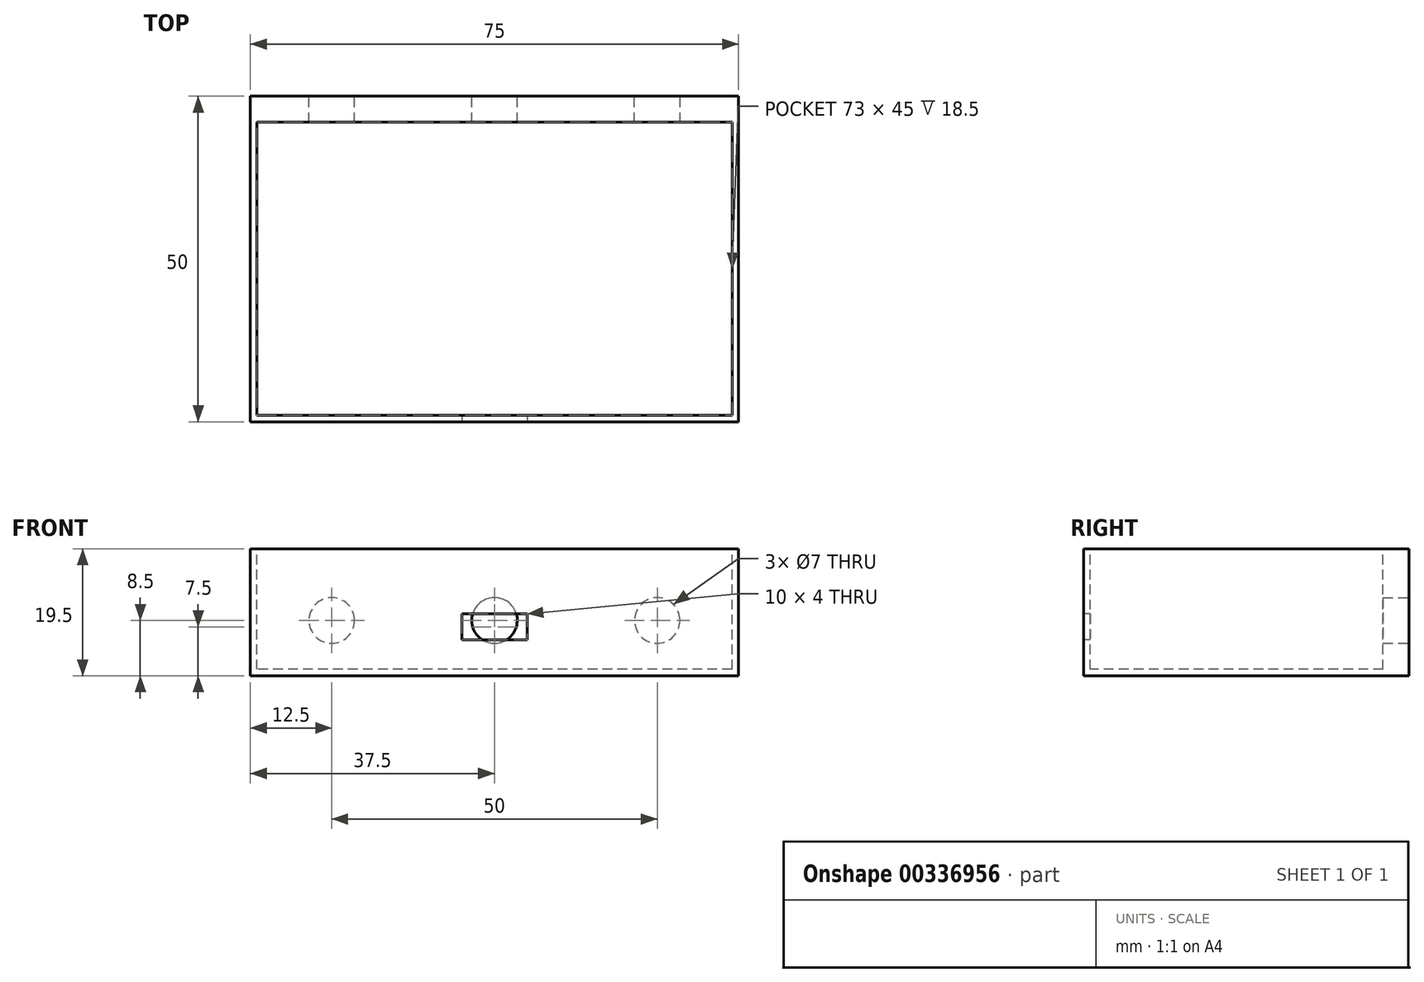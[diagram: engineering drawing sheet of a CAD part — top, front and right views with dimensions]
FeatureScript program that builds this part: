
annotation { "Feature Type Name" : "Feature", "Feature Type Description" : "" }
export const myFeature = defineFeature(function(context is Context, id is Id, definition is map)
    precondition{}
    {
        {
            assignVariable(context, id + "F0", {"name" : "floor_thickness", "anyValue" : 1});
        }
        {
            assignVariable(context, id + "F1", {"name" : "box_depth", "anyValue" : 17.5});
        }
        {
            var Q0;
            Q0=qCreatedBy(makeId("Top.planeOp"),FACE);
            var sketch = newSketch(context, id + "F2", { "sketchPlane" : qUnion([Q0])});
            skLineSegment(sketch, "E0.bottom", {"start": v(37.5, 25) * mm, "end": v(-37.5, 25) * mm});
            skLineSegment(sketch, "E0.top", {"start": v(37.5, -25) * mm, "end": v(-37.5, -25) * mm});
            skLineSegment(sketch, "E0.left", {"start": v(37.5, 25) * mm, "end": v(37.5, -25) * mm});
            skLineSegment(sketch, "E0.right", {"start": v(-37.5, 25) * mm, "end": v(-37.5, -25) * mm});
            skPoint(sketch, "E0.middle", {"position": v(0, 0) * mm});
            skSolve(sketch);
        }
        {
            var Q0;
            Q0 = qSketchRegion(id + "F2", true);
            extrude(context, id + "F3", {"entities" : qUnion([Q0]), "depth" : (getVariable(context, 'box_depth') + (getVariable(context, 'floor_thickness') * 2)) * mm});
        }
        {
            var Q0;
            Q0=makeQuery(id+"F3.opExtrude","CAP_FACE",FACE,{"disambiguationData":[OSD([sQuery(id+"F2.wireOp",EDGE,"E0.bottom"),sQuery(id+"F2.wireOp",EDGE,"E0.top"),sQuery(id+"F2.wireOp",EDGE,"E0.left"),sQuery(id+"F2.wireOp",EDGE,"E0.right")])],"isStart":false});
            var sketch = newSketch(context, id + "F4", { "sketchPlane" : qUnion([Q0])});
            skLineSegment(sketch, "E1.bottom", {"start": v(36.5, 21) * mm, "end": v(-36.5, 21) * mm});
            skLineSegment(sketch, "E1.top", {"start": v(36.5, -24) * mm, "end": v(-36.5, -24) * mm});
            skLineSegment(sketch, "E1.left", {"start": v(36.5, 21) * mm, "end": v(36.5, -24) * mm});
            skLineSegment(sketch, "E1.right", {"start": v(-36.5, 21) * mm, "end": v(-36.5, -24) * mm});
            skPoint(sketch, "E1.middle", {"position": v(0, 0) * mm});
            skSolve(sketch);
        }
        {
            var Q0;
            Q0=makeQuery(id+"F4.imprint","IMPRINT",FACE,{"disambiguationData":[TD([[makeQuery(id+"F4.imprint","IMPRINT",EDGE,{"derivedFrom":sQuery(id+"F4.wireOp",EDGE,"E1.bottom")}),1.0]])]});
            extrude(context, id + "F5", {"entities" : qUnion([Q0]), "operationType" : NewBodyOperationType.REMOVE, "oppositeDirection" : true, "depth" : (getVariable(context, 'box_depth') + getVariable(context, 'floor_thickness')) * mm});
        }
        {
            var Q0;
            Q0=makeQuery(id+"F3.opExtrude","SWEPT_FACE",FACE,{"disambiguationData":[OSD([sQuery(id+"F2.wireOp",EDGE,"E0.top")])]});
            var sketch = newSketch(context, id + "F6", { "sketchPlane" : qUnion([Q0])});
            skLineSegment(sketch, "E2", {"start": v(0, 0) * mm, "end": v(0, 7.5) * mm, "construction": true});
            skPoint(sketch, "E2.endSnap0", {"position": v(0, 0) * mm});
            skLineSegment(sketch, "E3.bottom", {"start": v(5, 9.5) * mm, "end": v(-5, 9.5) * mm});
            skLineSegment(sketch, "E3.top", {"start": v(5, 5.5) * mm, "end": v(-5, 5.5) * mm});
            skLineSegment(sketch, "E3.left", {"start": v(5, 9.5) * mm, "end": v(5, 5.5) * mm});
            skLineSegment(sketch, "E3.right", {"start": v(-5, 9.5) * mm, "end": v(-5, 5.5) * mm});
            skPoint(sketch, "E3.middle", {"position": v(0, 7.5) * mm});
            skSolve(sketch);
        }
        {
            var Q0;
            Q0=makeQuery(id+"F6.imprint","IMPRINT",FACE,{"disambiguationData":[TD([[makeQuery(id+"F6.imprint","IMPRINT",EDGE,{"derivedFrom":sQuery(id+"F6.wireOp",EDGE,"E3.bottom")}),1.0]])]});
            extrude(context, id + "F7", {"entities" : qUnion([Q0]), "operationType" : NewBodyOperationType.REMOVE, "endBound" : BoundingType.UP_TO_NEXT, "oppositeDirection" : true, "depth" : 25 * mm});
        }
        {
            var Q0;
            Q0=makeQuery(id+"F3.opExtrude","SWEPT_FACE",FACE,{"disambiguationData":[OSD([sQuery(id+"F2.wireOp",EDGE,"E0.bottom")])]});
            var sketch = newSketch(context, id + "F8", { "sketchPlane" : qUnion([Q0])});
            skLineSegment(sketch, "E4", {"start": v(0, 0) * mm, "end": v(0, 8.5) * mm, "construction": true});
            skLineSegment(sketch, "E5", {"start": v(0, 8.5) * mm, "end": v(25, 8.5) * mm, "construction": true});
            skLineSegment(sketch, "E6", {"start": v(0, 8.5) * mm, "end": v(-25, 8.5) * mm, "construction": true});
            skCircle(sketch, "E7", {"center": v(-25, 8.5) * mm, "radius": 3.5 * mm});
            skCircle(sketch, "E8", {"center": v(0, 8.5) * mm, "radius": 3.5 * mm});
            skCircle(sketch, "E9", {"center": v(25, 8.5) * mm, "radius": 3.5 * mm});
            skSolve(sketch);
        }
        {
            var Q0;
            Q0=makeQuery(id+"F8.imprint","IMPRINT",FACE,{"disambiguationData":[TD([[makeQuery(id+"F8.imprint","IMPRINT",EDGE,{"derivedFrom":sQuery(id+"F8.wireOp",EDGE,"E7")}),1.0]])]});
            var Q1;
            Q1=makeQuery(id+"F8.imprint","IMPRINT",FACE,{"disambiguationData":[TD([[makeQuery(id+"F8.imprint","IMPRINT",EDGE,{"derivedFrom":sQuery(id+"F8.wireOp",EDGE,"E8")}),1.0]])]});
            var Q2;
            Q2=makeQuery(id+"F8.imprint","IMPRINT",FACE,{"disambiguationData":[TD([[makeQuery(id+"F8.imprint","IMPRINT",EDGE,{"derivedFrom":sQuery(id+"F8.wireOp",EDGE,"E9")}),1.0]])]});
            extrude(context, id + "F9", {"entities" : qUnion([Q0, Q1, Q2]), "operationType" : NewBodyOperationType.REMOVE, "endBound" : BoundingType.UP_TO_NEXT, "oppositeDirection" : true, "depth" : 25 * mm});
        }
    });
